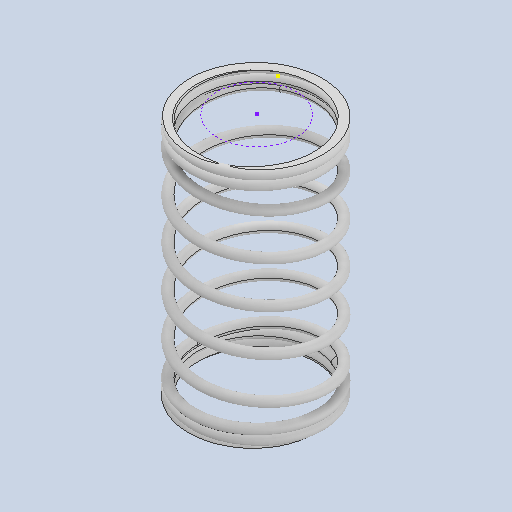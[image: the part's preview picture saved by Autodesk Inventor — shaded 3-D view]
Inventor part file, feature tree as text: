
AUTODESK INVENTOR PART (.ipt)
format: ipt  version: 2024 (Build 280153000, 153)  size: 937,472 bytes
history: native  units: in
note: dims shown in document units (in); Inventor stores cm internally (conversion verified against a paired STEP export)
features: sketch x6, helix x3, extrude x3, direct_edit x1, projected_geometry x1, other x1
ambient origin geometry x8: Origin, YZ Plane, XZ Plane, XY Plane, X Axis, Y Axis, Z Axis, Center Point
bodies: Solid1 (feature_tree)
feature tree (15):
  sketch  "Sketch1"  dims[d3=0.55in]
  helix  "Coil1"  [1 undecoded]
  helix  "Coil2"  [1 undecoded]
  extrude  "Extrusion1"  Depth=0.044in
  helix  "Coil3"  [1 undecoded]
  extrude  "Extrusion2"  Depth=1.0in TaperAngle=0.0deg
  extrude  "Extrusion3"  Depth=3.937in
  direct_edit  "Direct Edit1"
  sketch  "Sketch6"  dims[d32=1.0in d33=0.0in d34=3.937in d35=0.3937in d36=0.3937in]
  sketch  "Sketch2"  dims[d4=1.0in d5=1.0in d6=1.9685in d7=0.0in d8=30.0deg d9=0.0069in d10=30.0deg d11=0.0069in d12=0.044in]
  sketch  "Sketch3"  dims[d13=1.0in d14=0.7874in d15=0.0in d16=90.0deg d17=90.0deg d18=0.0in d19=0.0in d20=1.0in d21=0.0in]
  sketch  "Sketch4"  dims[d22=0.044in]
  sketch  "Sketch5"  dims[d23=1.0in d24=0.7874in d25=0.0in d26=90.0deg d27=90.0deg d28=0.0in d29=0.0in d30=1.0in d31=0.0in]
  projected_geometry  "Project Cut Edges1"
  other  "Scale1"
note: 3 required parameter values undecoded (feature->parameter linkage not recoverable at this tier; creation-order binding heuristic only, values carry confidence <= 0.55)
